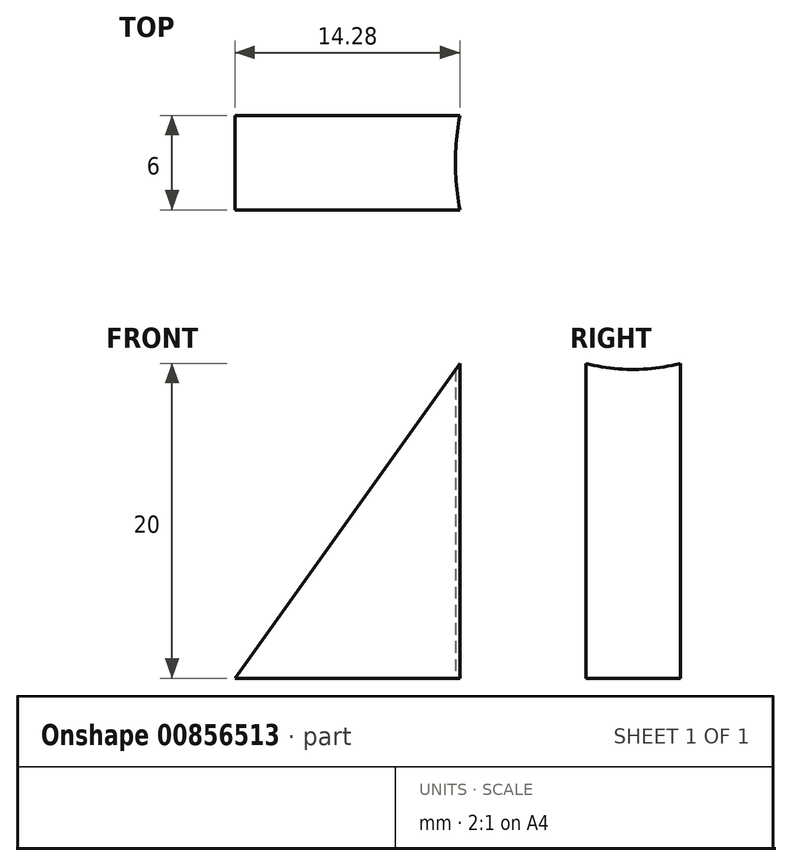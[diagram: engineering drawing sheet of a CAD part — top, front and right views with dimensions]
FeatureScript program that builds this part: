
annotation { "Feature Type Name" : "Feature", "Feature Type Description" : "" }
export const myFeature = defineFeature(function(context is Context, id is Id, definition is map)
    precondition{}
    {
        {
            var Q0;
            Q0=qCreatedBy(makeId("Top.planeOp"),FACE);
            var sketch = newSketch(context, id + "F0", { "sketchPlane" : qUnion([Q0])});
            skLineSegment(sketch, "E0.bottom", {"start": v(7.14, 3) * mm, "end": v(-7.14, 3) * mm});
            skLineSegment(sketch, "E0.top", {"start": v(7.14, -3) * mm, "end": v(-7.14, -3) * mm});
            skLineSegment(sketch, "E0.left", {"start": v(7.14, 3) * mm, "end": v(7.14, -3) * mm});
            skLineSegment(sketch, "E0.right", {"start": v(-7.14, 3) * mm, "end": v(-7.14, -3) * mm});
            skPoint(sketch, "E0.middle", {"position": v(0, 0) * mm});
            skPoint(sketch, "E1", {"position": v(7.14, 0) * mm});
            skSolve(sketch);
        }
        {
            var Q0;
            Q0=makeQuery(id+"F0.imprint","IMPRINT",FACE,{"disambiguationData":[TD([[makeQuery(id+"F0.imprint","IMPRINT",EDGE,{"derivedFrom":sQuery(id+"F0.wireOp",EDGE,"E0.bottom")}),1.0]])]});
            extrude(context, id + "F1", {"entities" : qUnion([Q0]), "depth" : 20 * mm, "offsetDistance" : 25 * mm});
        }
        {
            var Q0;
            Q0=makeQuery(id+"F1.opExtrude","CAP_EDGE",EDGE,{"disambiguationData":[OSD([sQuery(id+"F0.wireOp",EDGE,"E0.right")])],"isStart":false});
            chamfer(context, id + "F2", {"entities" : qUnion([Q0]), "chamferType" : ChamferType.TWO_OFFSETS, "width1" : 14.28 * mm, "oppositeDirection" : false, "width2" : 20 * mm, "tangentPropagation" : true});
        }
        {
            var Q0;
            Q0=qCreatedBy(makeId("Top.planeOp"),FACE);
            var sketch = newSketch(context, id + "F3", { "sketchPlane" : qUnion([Q0])});
            skPoint(sketch, "E2", {"position": v(0, 0) * mm});
            skPoint(sketch, "E3.0", {"position": v(7.14, 3) * mm});
            skCircle(sketch, "E4", {"center": v(7.14, 3) * mm, "radius": 16 * mm});
            skPoint(sketch, "E5.0", {"position": v(7.14, -3) * mm});
            skCircle(sketch, "E6", {"center": v(7.14, -3) * mm, "radius": 16 * mm});
            skPoint(sketch, "E7", {"position": v(22.86, 0) * mm});
            skCircle(sketch, "E8", {"center": v(22.86, 0) * mm, "radius": 16 * mm});
            skSolve(sketch);
        }
        {
            var Q0;
            Q0=sQuery(id+"F3.wireOp",VERTEX,"E8.center");
            var Q1;
            Q1=makeQuery(id+"F1.opExtrude","SWEPT_BODY",BODY,{"disambiguationData":[OSD([sQuery(id+"F0.wireOp",EDGE,"E0.bottom"),sQuery(id+"F0.wireOp",EDGE,"E0.top"),sQuery(id+"F0.wireOp",EDGE,"E0.left"),sQuery(id+"F0.wireOp",EDGE,"E0.right")])]});
            hole(context, id + "F4", {"style" : HoleStyle.SIMPLE, "endStyle" : HoleEndStyle.THROUGH, "oppositeDirection" : true, "holeDiameter" : 32 * mm, "majorDiameter" : 5 * mm, "isTappedThrough" : true, "tappedDepth" : 25 * mm, "tapClearance" : 3, "locations" : qUnion([Q0]), "scope" : qUnion([Q1])});
        }
    });
